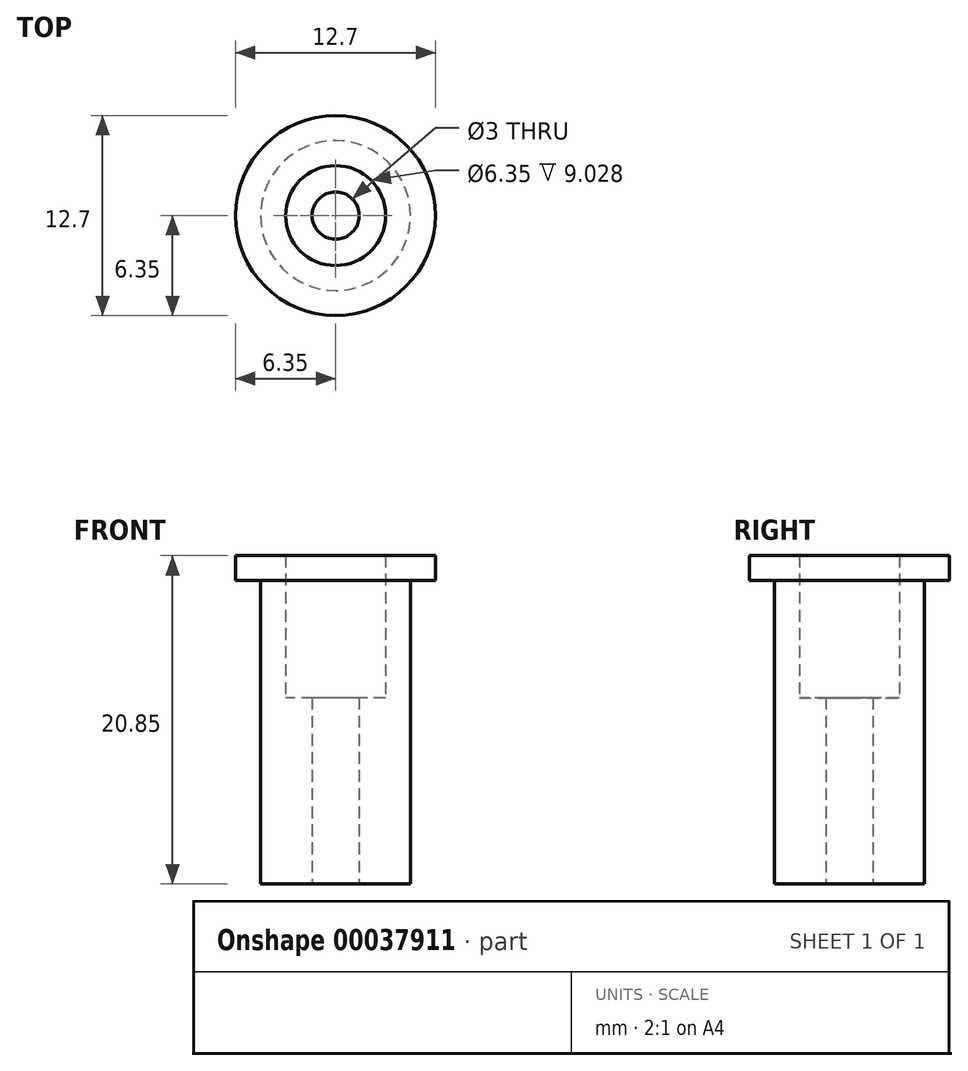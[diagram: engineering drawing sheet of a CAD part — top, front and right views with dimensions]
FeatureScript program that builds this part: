
annotation { "Feature Type Name" : "Feature", "Feature Type Description" : "" }
export const myFeature = defineFeature(function(context is Context, id is Id, definition is map)
    precondition{}
    {
        {
            var Q0;
            Q0=qCreatedBy(makeId("Top.planeOp"),FACE);
            var sketch = newSketch(context, id + "F0", { "sketchPlane" : qUnion([Q0])});
            skCircle(sketch, "E0", {"center": v(0, 0) * mm, "radius": 1.5 * mm});
            skCircle(sketch, "E1", {"center": v(0, 0) * mm, "radius": 4.76 * mm});
            skSolve(sketch);
        }
        {
            var Q0;
            Q0 = qSketchRegion(id + "F0", true);
            extrude(context, id + "F1", {"entities" : qUnion([Q0]), "depth" : 11.83 * mm});
        }
        {
            var Q0;
            Q0=makeQuery(id+"F1.opExtrude","CAP_FACE",FACE,{"disambiguationData":[OSD([sQuery(id+"F0.wireOp",EDGE,"E0"),sQuery(id+"F0.wireOp",EDGE,"E1")])],"isStart":false});
            var sketch = newSketch(context, id + "F2", { "sketchPlane" : qUnion([Q0])});
            skCircle(sketch, "E2", {"center": v(0, 0) * mm, "radius": 3.18 * mm});
            skCircle(sketch, "E3", {"center": v(0, 0) * mm, "radius": 4.76 * mm});
            skSolve(sketch);
        }
        {
            var Q0;
            Q0 = qSketchRegion(id + "F2", true);
            extrude(context, id + "F3", {"entities" : qUnion([Q0]), "operationType" : NewBodyOperationType.ADD, "depth" : 7.44 * mm});
        }
        {
            var Q0;
            Q0=makeQuery(id+"F3.opExtrude","CAP_FACE",FACE,{"disambiguationData":[OSD([sQuery(id+"F2.wireOp",EDGE,"E2"),sQuery(id+"F2.wireOp",EDGE,"E3")])],"isStart":false});
            var sketch = newSketch(context, id + "F4", { "sketchPlane" : qUnion([Q0])});
            skCircle(sketch, "E4", {"center": v(0, 0) * mm, "radius": 6.35 * mm});
            skCircle(sketch, "E5", {"center": v(0, 0) * mm, "radius": 3.18 * mm});
            skSolve(sketch);
        }
        {
            var Q0;
            Q0 = qSketchRegion(id + "F4", true);
            extrude(context, id + "F5", {"entities" : qUnion([Q0]), "operationType" : NewBodyOperationType.ADD, "depth" : 1.59 * mm});
        }
    });
